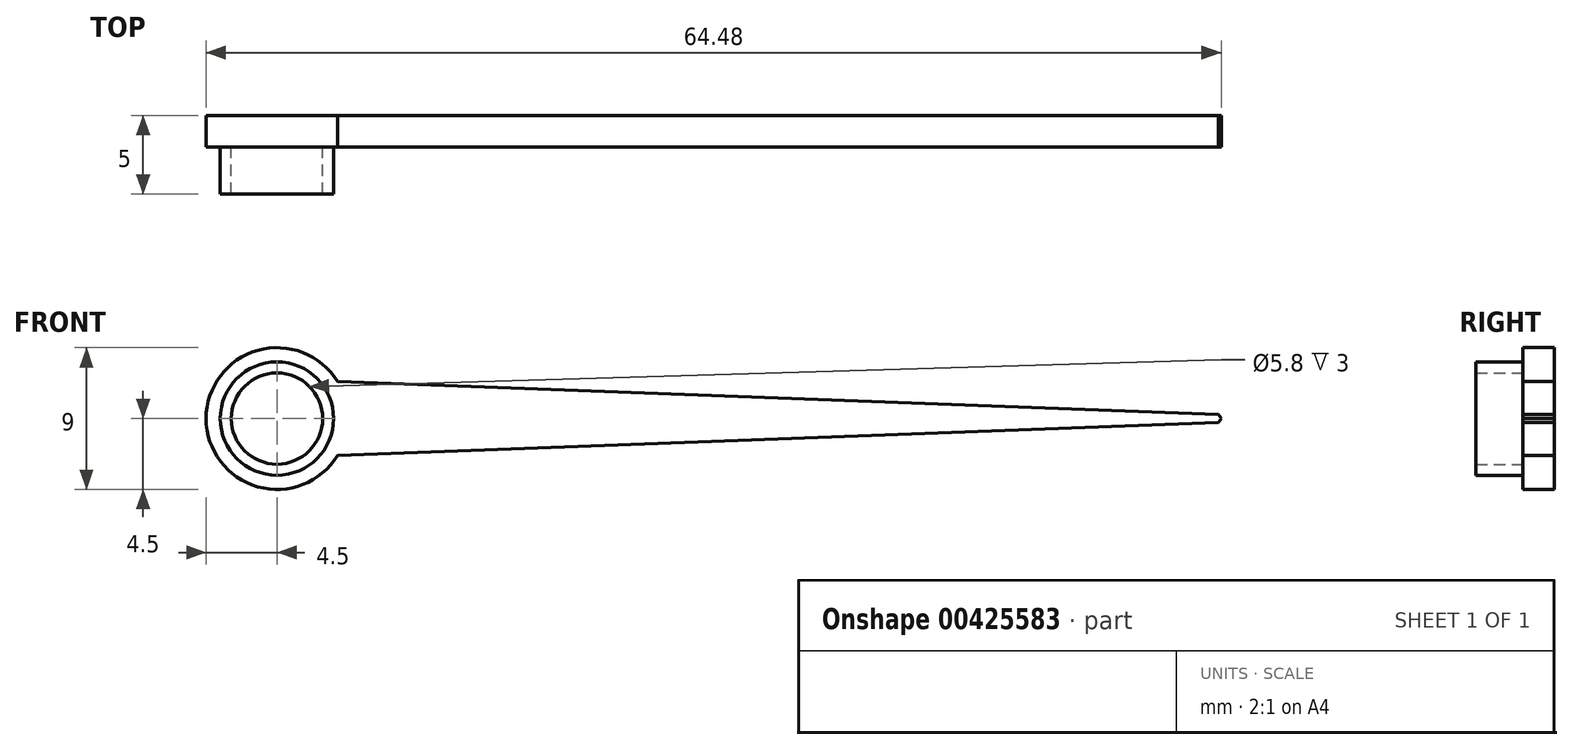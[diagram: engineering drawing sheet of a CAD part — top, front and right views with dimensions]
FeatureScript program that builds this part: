
annotation { "Feature Type Name" : "Feature", "Feature Type Description" : "" }
export const myFeature = defineFeature(function(context is Context, id is Id, definition is map)
    precondition{}
    {
        {
            var Q0;
            Q0=qCreatedBy(makeId("Front.planeOp"),FACE);
            var sketch = newSketch(context, id + "F0", { "sketchPlane" : qUnion([Q0])});
            skCircle(sketch, "E0", {"center": v(0, 0) * mm, "radius": 4.5 * mm});
            skLineSegment(sketch, "E1", {"start": v(0, 0) * mm, "end": v(60, 0) * mm, "construction": true});
            skLineSegment(sketch, "E2", {"start": v(3.84, 4.76) * mm, "end": v(3.84, -5.16) * mm, "construction": true});
            skPoint(sketch, "E3.center.orphan", {"position": v(30, 0) * mm});
            skLineSegment(sketch, "E4", {"start": v(59.8, 0.26) * mm, "end": v(59.98, 0) * mm});
            skLineSegment(sketch, "E5", {"start": v(59.98, 0) * mm, "end": v(59.8, -0.26) * mm});
            skLineSegment(sketch, "E6", {"start": v(3.84, 2.35) * mm, "end": v(59.8, 0.26) * mm});
            skLineSegment(sketch, "E7", {"start": v(3.84, -2.35) * mm, "end": v(59.8, -0.26) * mm});
            skSolve(sketch);
        }
        {
            var Q0;
            {var subQ0=sQuery(id+"F0.wireOp",EDGE,"E0");var subQ1=makeQuery(id+"F0.imprint","INTERSECT",VERTEX,{"derivedFrom":[subQ0,sQuery(id+"F0.wireOp",EDGE,"fq5BQrI3-vk30-LFix-EeT1-IGketQb3BoCO")]});Q0=makeQuery(id+"F0.imprint","IMPRINT",FACE,{"disambiguationData":[TD([[makeQuery(id+"F0.imprint","IMPRINT",EDGE,{"disambiguationData":[TD([[subQ1,-1.0]])],"derivedFrom":subQ0}),1.0]])]});}
            var Q1;
            {var subQ0=sQuery(id+"F0.wireOp",EDGE,"fq5BQrI3-vk30-LFix-EeT1-IGketQb3BoCO");Q1=makeQuery(id+"F0.imprint","IMPRINT",FACE,{"disambiguationData":[TD([[makeQuery(id+"F0.imprint","IMPRINT",EDGE,{"derivedFrom":subQ0}),-1.0]])]});}
            var Q2;
            {var subQ0=sQuery(id+"F0.wireOp",EDGE,"E3");var subQ1=makeQuery(id+"F0.imprint","INTERSECT",VERTEX,{"derivedFrom":[sQuery(id+"F0.wireOp",EDGE,"fq5BQrI3-vk30-LFix-EeT1-IGketQb3BoCO"),subQ0]});Q2=makeQuery(id+"F0.imprint","IMPRINT",FACE,{"disambiguationData":[TD([[makeQuery(id+"F0.imprint","IMPRINT",EDGE,{"disambiguationData":[TD([[subQ1,1.0]])],"derivedFrom":subQ0}),1.0]])]});}
            var Q3;
            {var subQ0=sQuery(id+"F0.wireOp",EDGE,"QLxc27Nm-pPKZ-rbCJ-c22z-aktoqo1wA93M");Q3=makeQuery(id+"F0.imprint","IMPRINT",FACE,{"disambiguationData":[TD([[makeQuery(id+"F0.imprint","IMPRINT",EDGE,{"derivedFrom":subQ0}),-1.0]])]});}
            extrude(context, id + "F1", {"entities" : qUnion([Q0, Q1, Q2, Q3]), "depth" : 2 * mm, "symmetric" : true});
        }
        {
            var Q0;
            Q0=makeQuery(id+"F1.opExtrude","CAP_FACE",FACE,{"disambiguationData":[OSD([sQuery(id+"F0.wireOp",EDGE,"E0"),sQuery(id+"F0.wireOp",EDGE,"fq5BQrI3-vk30-LFix-EeT1-IGketQb3BoCO"),sQuery(id+"F0.wireOp",EDGE,"QLxc27Nm-pPKZ-rbCJ-c22z-aktoqo1wA93M"),sQuery(id+"F0.wireOp",EDGE,"E3"),sQuery(id+"F0.wireOp",EDGE,"ce6365be-2cfe-4bbf-9333-eff700ed5db3.trimOffspring"),sQuery(id+"F0.wireOp",EDGE,"ae82a7dc-09e3-4c30-b862-928eb51e0c18.trimOffspring"),sQuery(id+"F0.wireOp",EDGE,"IuADU5Em-Ggmq-a5Qv-uISl-qxMzmkECTUyd")])],"isStart":true});
            var sketch = newSketch(context, id + "F2", { "sketchPlane" : qUnion([Q0])});
            skCircle(sketch, "E8", {"center": v(0, 0) * mm, "radius": 3.6 * mm});
            skCircle(sketch, "E9", {"center": v(0, 0) * mm, "radius": 2.9 * mm});
            skSolve(sketch);
        }
        {
            var Q0;
            Q0=makeQuery(id+"F2.imprint","IMPRINT",FACE,{"disambiguationData":[TD([[makeQuery(id+"F2.imprint","IMPRINT",EDGE,{"derivedFrom":sQuery(id+"F2.wireOp",EDGE,"E8")}),1.0]])]});
            extrude(context, id + "F3", {"entities" : qUnion([Q0]), "operationType" : NewBodyOperationType.ADD, "oppositeDirection" : true, "depth" : 5 * mm});
        }
        {
            var Q0;
            Q0=makeQuery(id+"F0.imprint","IMPRINT",FACE,{"disambiguationData":[TD([[makeQuery(id+"F0.imprint","IMPRINT",EDGE,{"derivedFrom":sQuery(id+"F0.wireOp",EDGE,"E4")}),-1.0]])]});
            extrude(context, id + "F4", {"entities" : qUnion([Q0]), "operationType" : NewBodyOperationType.ADD, "depth" : 2 * mm, "symmetric" : true});
        }
    });
